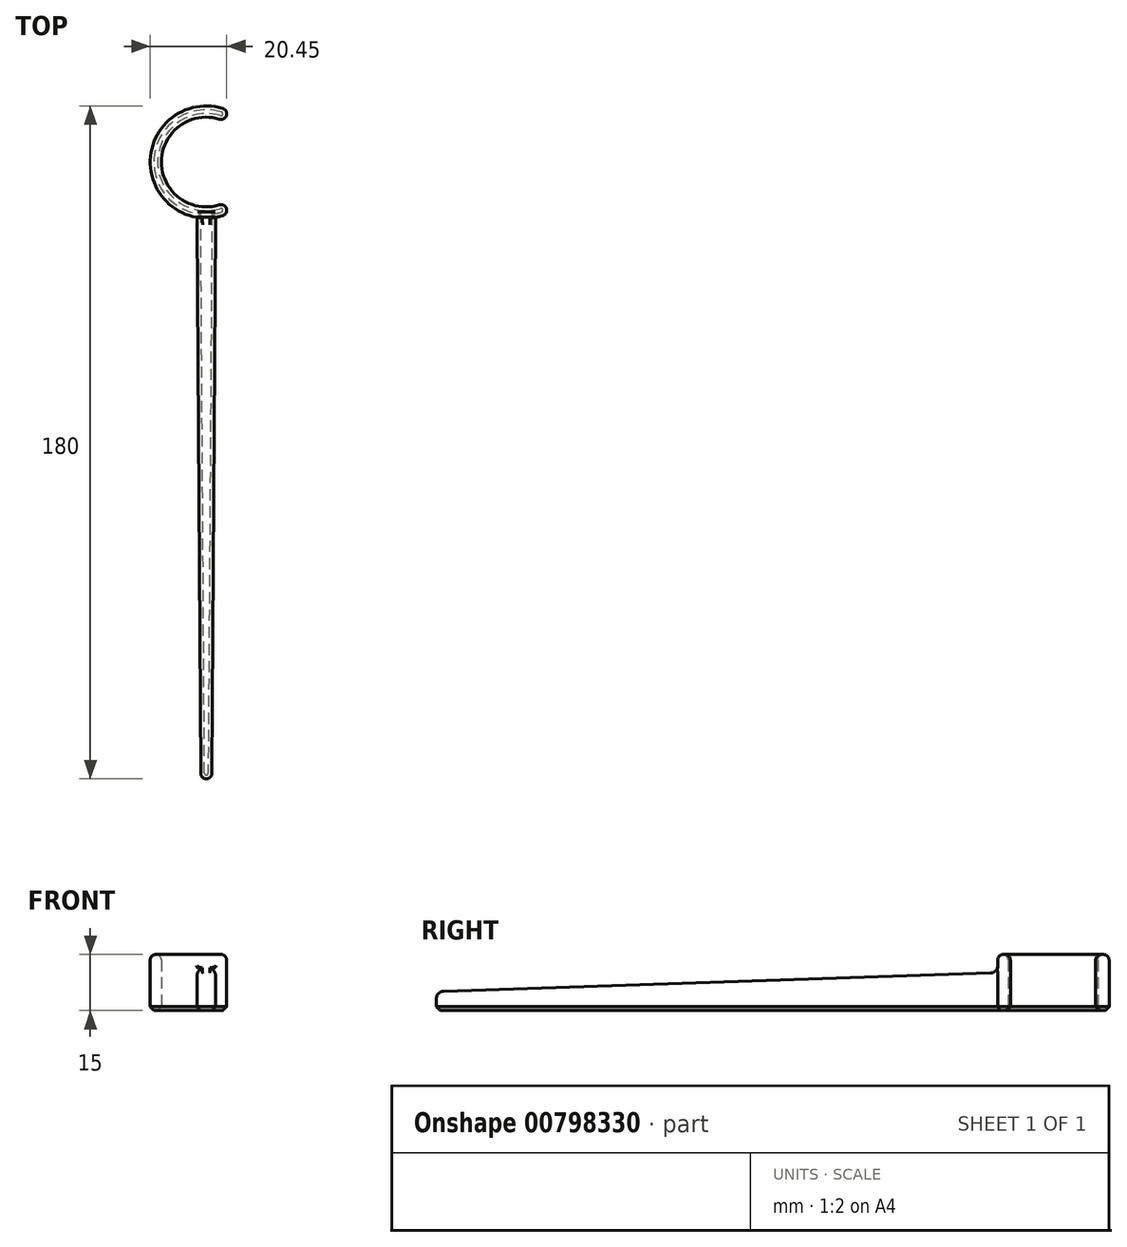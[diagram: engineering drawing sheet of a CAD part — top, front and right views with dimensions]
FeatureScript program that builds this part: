
annotation { "Feature Type Name" : "Feature", "Feature Type Description" : "" }
export const myFeature = defineFeature(function(context is Context, id is Id, definition is map)
    precondition{}
    {
        {
            var Q0;
            Q0=qCreatedBy(makeId("Top.planeOp"),FACE);
            var sketch = newSketch(context, id + "F0", { "sketchPlane" : qUnion([Q0])});
            skCircle(sketch, "E0", {"center": v(0, 0) * mm, "radius": 12 * mm});
            skCircle(sketch, "E1", {"center": v(0, 0) * mm, "radius": 15 * mm});
            skArc(sketch, "E2", {"start": v(3.51, 11.47) * mm, "mid": v(5.39, 12.47) * mm, "end": v(4.4, 14.34) * mm});
            skArc(sketch, "E3", {"start": v(4.4, -14.34) * mm, "mid": v(5.39, -12.47) * mm, "end": v(3.51, -11.47) * mm});
            skCircle(sketch, "E4", {"center": v(0, -163.5) * mm, "radius": 1.5 * mm});
            skLineSegment(sketch, "E5", {"start": v(-2.5, -14.8) * mm, "end": v(-1.5, -163.51) * mm});
            skLineSegment(sketch, "E6", {"start": v(1.5, -163.51) * mm, "end": v(2.5, -14.8) * mm});
            skSolve(sketch);
        }
        {
            var Q0;
            {var subQ0=sQuery(id+"F0.wireOp",EDGE,"E5");Q0=makeQuery(id+"F0.imprint","IMPRINT",FACE,{"disambiguationData":[TD([[makeQuery(id+"F0.imprint","IMPRINT",EDGE,{"derivedFrom":subQ0}),1.0]])]});}
            var Q1;
            {var subQ4=sQuery(id+"F0.wireOp",EDGE,"E2");Q1=makeQuery(id+"F0.imprint","IMPRINT",FACE,{"disambiguationData":[TD([[makeQuery(id+"F0.imprint","IMPRINT",EDGE,{"derivedFrom":subQ4}),1.0]])]});}
            var Q2;
            {var subQ0=sQuery(id+"F0.wireOp",EDGE,"E4");var subQ1=makeQuery(id+"F0.imprint","INTERSECT",VERTEX,{"derivedFrom":[subQ0,sQuery(id+"F0.wireOp",EDGE,"E5")]});Q2=makeQuery(id+"F0.imprint","IMPRINT",FACE,{"disambiguationData":[TD([[makeQuery(id+"F0.imprint","IMPRINT",EDGE,{"disambiguationData":[TD([[subQ1,-1.0]])],"derivedFrom":subQ0}),1.0]])]});}
            extrude(context, id + "F1", {"entities" : qUnion([Q0, Q1, Q2]), "depth" : 15 * mm, "offsetDistance" : 25 * mm});
        }
        {
            var Q0;
            Q0=qCreatedBy(makeId("Right.planeOp"),FACE);
            var sketch = newSketch(context, id + "F2", { "sketchPlane" : qUnion([Q0])});
            skLineSegment(sketch, "E7.0", {"start": v(-163.5, 15) * mm, "end": v(-14.8, 15) * mm});
            skLineSegment(sketch, "E8.0", {"start": v(-14.8, 15) * mm, "end": v(-14.8, 12.03) * mm});
            skLineSegment(sketch, "E9.0.0", {"start": v(-163.5, 0) * mm, "end": v(-163.5, 0) * mm});
            skLineSegment(sketch, "E9.0.2", {"start": v(-163.5, 15) * mm, "end": v(-165, 15) * mm});
            skLineSegment(sketch, "E9.0.3", {"start": v(-163.51, 15) * mm, "end": v(-163.51, 0) * mm});
            skLineSegment(sketch, "E10", {"start": v(-163.07, 5.17) * mm, "end": v(-16.72, 10.04) * mm});
            skLineSegment(sketch, "E11", {"start": v(-14.8, 0) * mm, "end": v(-163.5, 0) * mm});
            skArc(sketch, "E12.filletArc", {"start": v(-163.07, 5.17) * mm, "mid": v(-164.44, 4.56) * mm, "end": v(-165, 3.17) * mm});
            skPoint(sketch, "E13", {"position": v(-14.8, 7.5) * mm});
            skPoint(sketch, "E14.newPointA", {"position": v(-14.8, 10.1) * mm});
            skPoint(sketch, "E14.newPointB", {"position": v(-14.8, 0) * mm});
            skArc(sketch, "E14.filletArc", {"start": v(-16.72, 10.04) * mm, "mid": v(-15.35, 10.64) * mm, "end": v(-14.8, 12.03) * mm});
            skLineSegment(sketch, "E15", {"start": v(-165, 15) * mm, "end": v(-14.8, 15) * mm});
            skLineSegment(sketch, "E16", {"start": v(-165, 3.17) * mm, "end": v(-165, 15) * mm});
            skLineSegment(sketch, "E17", {"start": v(-163.5, 0) * mm, "end": v(-165, 0) * mm});
            skLineSegment(sketch, "E18", {"start": v(-165, 0) * mm, "end": v(-165, 3.17) * mm});
            skSolve(sketch);
        }
        {
            var Q0;
            {var subQ6=sQuery(id+"F2.wireOp",EDGE,"E8.0");Q0=makeQuery(id+"F2.imprint","IMPRINT",FACE,{"disambiguationData":[TD([[makeQuery(id+"F2.imprint","IMPRINT",EDGE,{"derivedFrom":subQ6}),-1.0]])]});}
            var Q1;
            {var subQ5=sQuery(id+"F2.wireOp",EDGE,"E16");Q1=makeQuery(id+"F2.imprint","IMPRINT",FACE,{"disambiguationData":[TD([[makeQuery(id+"F2.imprint","IMPRINT",EDGE,{"derivedFrom":subQ5}),-1.0]])]});}
            extrude(context, id + "F3", {"entities" : qUnion([Q0, Q1]), "operationType" : NewBodyOperationType.REMOVE, "endBound" : BoundingType.SYMMETRIC, "oppositeDirection" : true, "depth" : 25 * mm, "offsetDistance" : 25 * mm});
        }
        {
            var Q0;
            Q0=makeQuery(id+"F3.boolean.opBoolean","COPY",FACE,{"derivedFrom":makeQuery(id+"F3.opExtrude","SWEPT_FACE",FACE,{"disambiguationData":[OSD([sQuery(id+"F2.wireOp",EDGE,"E10")])]})});
            var Q1;
            Q1=makeQuery(id+"F3.boolean.opBoolean","COPY",FACE,{"derivedFrom":makeQuery(id+"F3.opExtrude","SWEPT_FACE",FACE,{"disambiguationData":[OSD([sQuery(id+"F2.wireOp",EDGE,"E12.filletArc")])]})});
            var Q2;
            Q2=makeQuery(id+"F3.boolean.opBoolean","COPY",FACE,{"derivedFrom":makeQuery(id+"F3.opExtrude","SWEPT_FACE",FACE,{"disambiguationData":[OSD([sQuery(id+"F2.wireOp",EDGE,"E14.filletArc")])]})});
            var Q3;
            Q3=makeQuery(id+"F1.opExtrude","CAP_FACE",FACE,{"disambiguationData":[OSD([sQuery(id+"F0.wireOp",EDGE,"E0"),sQuery(id+"F0.wireOp",EDGE,"E1"),sQuery(id+"F0.wireOp",EDGE,"E2"),sQuery(id+"F0.wireOp",EDGE,"E3"),sQuery(id+"F0.wireOp",EDGE,"E4"),sQuery(id+"F0.wireOp",EDGE,"E5"),sQuery(id+"F0.wireOp",EDGE,"E6")])],"isStart":false});
            fillet(context, id + "F4", {"entities" : qUnion([Q0, Q1, Q2, Q3]), "radius" : 1.5 * mm, "tangentPropagation" : true, "allowEdgeOverflow" : false});
        }
        {
            var Q0;
            Q0=makeQuery(id+"F1.opExtrude","CAP_FACE",FACE,{"disambiguationData":[OSD([sQuery(id+"F0.wireOp",EDGE,"E0"),sQuery(id+"F0.wireOp",EDGE,"E1"),sQuery(id+"F0.wireOp",EDGE,"E2"),sQuery(id+"F0.wireOp",EDGE,"E3"),sQuery(id+"F0.wireOp",EDGE,"E4"),sQuery(id+"F0.wireOp",EDGE,"E5"),sQuery(id+"F0.wireOp",EDGE,"E6")])],"isStart":true});
            chamfer(context, id + "F5", {"entities" : qUnion([Q0]), "width" : 1 * mm, "tangentPropagation" : true});
        }
    });
